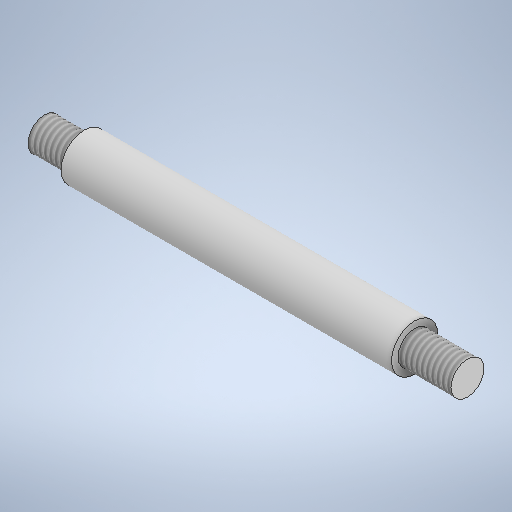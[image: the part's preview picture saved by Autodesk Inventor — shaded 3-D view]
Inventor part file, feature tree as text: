
AUTODESK INVENTOR PART (.ipt)
format: ipt  version: 2025.1 (Build 291241000, 241)  size: 266,240 bytes
history: native  units: mm
features: thread x2, revolve x1, sketch x1
ambient origin geometry x8: Origin, YZ Plane, XZ Plane, XY Plane, X Axis, Y Axis, Z Axis, Center Point
bodies: Solid1 (feature_tree)
feature tree (4):
  revolve  "Revolution1"  [1 undecoded]
  thread  "Thread1"  [1 undecoded]
  thread  "Thread2"  [1 undecoded]
  sketch  "Sketch1"  dims[d0=5.0mm d1=7.0mm d2=8.0mm d3=6.0mm d4=50.0mm d5=90.0deg d6=6.0mm d7=0.0mm d8=8.0mm d9=0.0mm]
note: 3 required parameter values undecoded (feature->parameter linkage not recoverable at this tier; creation-order binding heuristic only, values carry confidence <= 0.55)